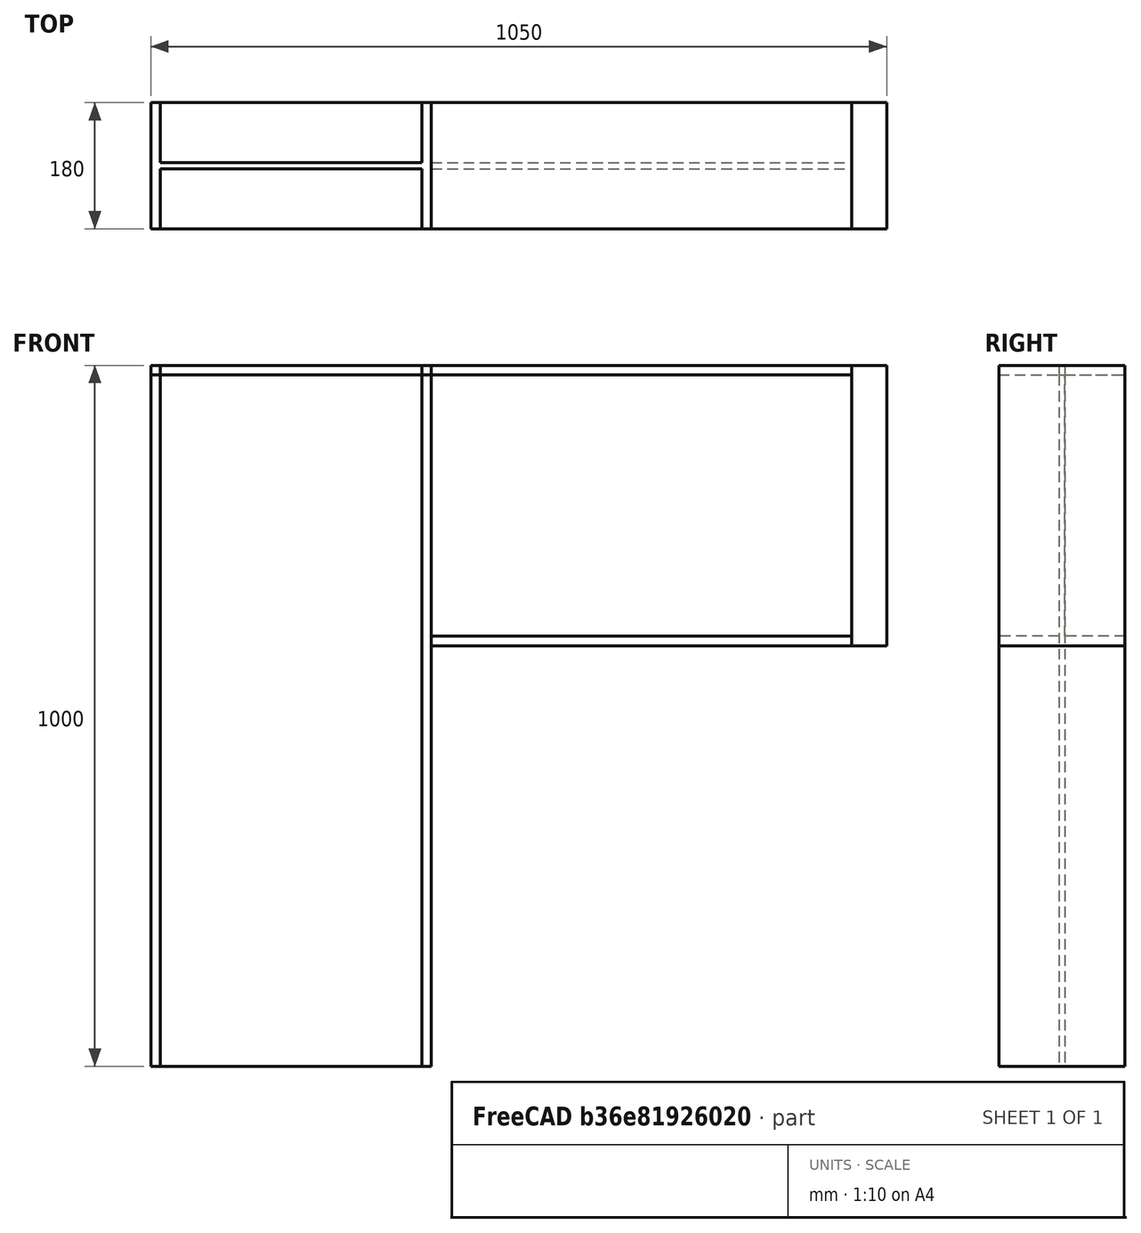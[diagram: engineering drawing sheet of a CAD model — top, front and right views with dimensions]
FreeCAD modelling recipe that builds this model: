
FCSTD DOCUMENT  (FreeCAD 0.21R33771 (Git))
Label: IPE400_3
License: All rights reserved
LicenseURL: http://en.wikipedia.org/wiki/All_rights_reserved
objects: Sketcher::SketchObject×2, Part::Extrusion×2, Part::Box×2, Fem::ConstraintForce×2, Fem::ConstraintFixed×1, App::MaterialObjectPython×1, Fem::FemSolverObjectPython×1, Fem::ConstraintDisplacement×1, Part::FeaturePython×1, Fem::FemMeshObjectPython×1, Fem::FemAnalysis×1
note: 7 computed .brp shape members not serialized (recipe doc carries the construction recipe); baked Part::Feature solids carry a one-line shape summary decoded from their .brp

FEATURE [Sketcher::SketchObject] Sketch
  FullyConstrained = true
  Placement = pos=(0,0,0) rot=(0.57735,0.57735,0.57735;2.0944rad)
  sketch-geometry (12):
    g0: LineSegment StartX=0 StartY=0 StartZ=0 EndX=180 EndY=0 EndZ=0
    g1: LineSegment StartX=180 StartY=0 StartZ=0 EndX=180 EndY=13.5 EndZ=0
    g2: LineSegment StartX=180 StartY=13.5 StartZ=0 EndX=94.3 EndY=13.5 EndZ=0
    g3: LineSegment StartX=94.3 StartY=13.5 StartZ=0 EndX=94.3 EndY=386.5 EndZ=0
    g4: LineSegment StartX=94.3 StartY=386.5 StartZ=0 EndX=180 EndY=386.5 EndZ=0
    g5: LineSegment StartX=180 StartY=386.5 StartZ=0 EndX=180 EndY=400 EndZ=0
    g6: LineSegment StartX=180 StartY=400 StartZ=0 EndX=0 EndY=400 EndZ=0
    g7: LineSegment StartX=0 StartY=400 StartZ=0 EndX=0 EndY=386.5 EndZ=0
    g8: LineSegment StartX=0 StartY=386.5 StartZ=0 EndX=85.7 EndY=386.5 EndZ=0
    g9: LineSegment StartX=85.7 StartY=386.5 StartZ=0 EndX=85.7 EndY=13.5 EndZ=0
    g10: LineSegment StartX=85.7 StartY=13.5 StartZ=0 EndX=0 EndY=13.5 EndZ=0
    g11: LineSegment StartX=0 StartY=13.5 StartZ=0 EndX=0 EndY=0 EndZ=0
  constraints (35):
    c: Coincident(g-1,g0)
    c: PointOnObject(g0,g-1)
    c: Coincident(g0,g1)
    c: Vertical(g1)
    c: Coincident(g1,g2)
    c: Horizontal(g2)
    c: Coincident(g2,g3)
    c: Vertical(g3)
    c: Coincident(g3,g4)
    c: Horizontal(g4)
    c: Coincident(g4,g5)
    c: Vertical(g5)
    c: Coincident(g5,g6)
    c: Horizontal(g6)
    c: Coincident(g6,g7)
    c: Vertical(g7)
    c: Coincident(g7,g8)
    c: Horizontal(g8)
    c: Coincident(g8,g9)
    c: Vertical(g9)
    c: Coincident(g9,g10)
    c: Horizontal(g10)
    c: Coincident(g10,g11)
    c: Coincident(g11,g0)
    c: DistanceX(g0,g0) = 180
    c: DistanceX(g6,g6) = 180
    c: PointOnObject(g6,g-2)
    c: Vertical(g11)
    c: DistanceX(g2,g2) = 85.7
    c: Equal(g10,g2)
    c: DistanceY(g11,g11) = 13.5
    c: Equal(g11,g1)
    c: Equal(g11,g7)
    c: Equal(g11,g5)
    c: DistanceY(g0,g6) = 400
FEATURE [Part::Extrusion] Extrude
  Base = -> Sketch
  Dir = (1,0,0)
  DirMode = 2
  FaceMakerClass = Part::FaceMakerBullseye
  LengthFwd = 600
  LengthRev = 0
  Solid = true
  Symmetric = false
FEATURE [Sketcher::SketchObject] Sketch001
  FullyConstrained = true
  Placement = pos=(0,0,0) rot=(0.57735,0.57735,0.57735;2.0944rad)
  sketch-geometry (12):
    g0: LineSegment StartX=0 StartY=0 StartZ=0 EndX=180 EndY=0 EndZ=0
    g1: LineSegment StartX=180 StartY=0 StartZ=0 EndX=180 EndY=13.5 EndZ=0
    g2: LineSegment StartX=180 StartY=13.5 StartZ=0 EndX=94.3 EndY=13.5 EndZ=0
    g3: LineSegment StartX=94.3 StartY=13.5 StartZ=0 EndX=94.3 EndY=386.5 EndZ=0
    g4: LineSegment StartX=94.3 StartY=386.5 StartZ=0 EndX=180 EndY=386.5 EndZ=0
    g5: LineSegment StartX=180 StartY=386.5 StartZ=0 EndX=180 EndY=400 EndZ=0
    g6: LineSegment StartX=180 StartY=400 StartZ=0 EndX=0 EndY=400 EndZ=0
    g7: LineSegment StartX=0 StartY=400 StartZ=0 EndX=0 EndY=386.5 EndZ=0
    g8: LineSegment StartX=0 StartY=386.5 StartZ=0 EndX=85.7 EndY=386.5 EndZ=0
    g9: LineSegment StartX=85.7 StartY=386.5 StartZ=0 EndX=85.7 EndY=13.5 EndZ=0
    g10: LineSegment StartX=85.7 StartY=13.5 StartZ=0 EndX=0 EndY=13.5 EndZ=0
    g11: LineSegment StartX=0 StartY=13.5 StartZ=0 EndX=0 EndY=0 EndZ=0
  constraints (35):
    c: Coincident(g-1,g0)
    c: PointOnObject(g0,g-1)
    c: Coincident(g0,g1)
    c: Vertical(g1)
    c: Coincident(g1,g2)
    c: Horizontal(g2)
    c: Coincident(g2,g3)
    c: Vertical(g3)
    c: Coincident(g3,g4)
    c: Horizontal(g4)
    c: Coincident(g4,g5)
    c: Vertical(g5)
    c: Coincident(g5,g6)
    c: Horizontal(g6)
    c: Coincident(g6,g7)
    c: Vertical(g7)
    c: Coincident(g7,g8)
    c: Horizontal(g8)
    c: Coincident(g8,g9)
    c: Vertical(g9)
    c: Coincident(g9,g10)
    c: Horizontal(g10)
    c: Coincident(g10,g11)
    c: Coincident(g11,g0)
    c: DistanceX(g0,g0) = 180
    c: DistanceX(g6,g6) = 180
    c: PointOnObject(g6,g-2)
    c: Vertical(g11)
    c: DistanceX(g2,g2) = 85.7
    c: Equal(g10,g2)
    c: DistanceY(g11,g11) = 13.5
    c: Equal(g11,g1)
    c: Equal(g11,g7)
    c: Equal(g11,g5)
    c: DistanceY(g0,g6) = 400
FEATURE [Part::Extrusion] Extrude001
  Base = -> Sketch001
  Dir = (1,0,0)
  DirMode = 2
  FaceMakerClass = Part::FaceMakerBullseye
  LengthFwd = 1000
  LengthRev = 0
  Placement = pos=(-400,0,400) rot=(0,1,0;1.5708rad)
  Solid = true
  Symmetric = false
FEATURE [Part::Box] Box  label="Cube"
  AttacherType = Attacher::AttachEngine3D
  Height = 400
  Length = 50
  Placement = pos=(600,0,0) rot=(0,0,1;0rad)
  Width = 180
FEATURE [Fem::ConstraintForce] ConstraintForce
  Direction = -> Box [Edge12]
  DirectionVector = (1,0,0)
  Force = 1000000
  NormalDirection = (0,0,1)
  Points = (16) [(600,0,400),(616.667,0,400),(633.333,0,400),(650,0,400),(600,60,400),(616.667,60,400),(633.333,60,400),(650,60,400),(600,120,400),(616.667,120,400),+6 more]
  References = -> [Box]
  Scale = 11
FEATURE [Fem::ConstraintFixed] ConstraintFixed
  NormalDirection = (0,0,-1)
  Normals = (8) [(0,0,-1),(0,0,-1),(0,0,-1),(0,0,-1),(0,0,-1),(0,0,-1),(0,0,-1),(0,0,-1)]
  Points = (8) [(-400,180,-600),(0,180,-600),(-400,120,-600),(0,120,-600),(-400,60,-600),(0,60,-600),(-400,0,-600),(0,0,-600)]
  References = -> [Extrude001]
  Scale = 18
FEATURE [App::MaterialObjectPython] MaterialSolid  # material (typed FeaturePython)
  Category = 0
  Material = AuthorAndLicense=(c) 2014 M. Münch - GNU Lesser General Public License (LGPL),CardName=Steel-15CrNi6,Density=7800 kg/m^3,+16 more (map truncated)
FEATURE [Fem::ConstraintForce] ConstraintForce001
  Direction = -> Box [Edge9]
  DirectionVector = (-1,0,0)
  Force = 1000000
  NormalDirection = (0,0,-1)
  Points = (16) [(600,0,0),(616.667,0,0),(633.333,0,0),(650,0,0),(600,60,0),(616.667,60,0),(633.333,60,0),(650,60,0),(600,120,0),(616.667,120,0),(633.333,120,0),+5 more]
  References = -> [Box]
  Reversed = true
  Scale = 11
FEATURE [Fem::FemSolverObjectPython] SolverCcxTools  # FEM object (typed FeaturePython)
  AnalysisType = 0
  BeamShellResultOutput3D = false
  BucklingFactors = 1
  EigenmodeHighLimit = 1000000
  EigenmodeLowLimit = 0
  EigenmodesCount = 10
  GeometricalNonlinearity = 0
  IterationsControlParameterCutb = 0.25,0.5,0.75,0.85,,,1.5,
  IterationsControlParameterIter = 4,8,9,200,10,400,,200,,
  IterationsControlParameterTimeUse = false
  IterationsThermoMechMaximum = 2000
  IterationsUserDefinedIncrementations = false
  IterationsUserDefinedTimeStepLength = false
  MaterialNonlinearity = 0
  MatrixSolverType = 0
  SplitInputWriter = false
  ThermoMechSteadyState = true
  TimeEnd = 1
  TimeInitialStep = 0.01
FEATURE [Fem::ConstraintDisplacement] ConstraintDisplacement
  NormalDirection = (0,1,0)
  Normals = (16) [(0,1,0),(0,1,0),(0,1,0),(0,1,0),(0,1,0),(0,1,0),(0,1,0),(0,1,0),(0,1,0),(0,1,0),(0,1,0),(0,1,0),(0,1,0),(0,1,0),(0,1,0),(0,1,0)]
  Points = (16) [(600,180,0),(600,180,133.333),(600,180,266.667),(600,180,400),(616.667,180,0),(616.667,180,133.333),(616.667,180,266.667),(616.667,180,400),+8 more]
  References = -> [Box]
  Scale = 16
  hasXFormula = false
  hasYFormula = false
  hasZFormula = false
  rotxFix = false
  rotxFree = true
  rotyFix = false
  rotyFree = true
  rotzFix = false
  rotzFree = true
  useFlowSurfaceForce = false
  xDisplacement = 0
  xFix = false
  xFree = true
  xRotation = 0
  yDisplacement = 0
  yFix = false
  yFree = false
  yRotation = 0
  zDisplacement = 0
  zFix = false
  zFree = true
  zRotation = 0
FEATURE [Part::Box] Box002  label="Cube002"
  AttacherType = Attacher::AttachEngine3D
  Height = 13.5
  Length = 400
  Placement = pos=(-400,0,386.5) rot=(0,0,1;0rad)
  Width = 180
FEATURE [Part::FeaturePython] BooleanFragments  # WARN: FeaturePython — macro-defined, semantics opaque (R4)
  Mode = 2
  Objects = -> [Extrude,Extrude001,Box,Box002]
  Tolerance = 0
FEATURE [Fem::FemMeshObjectPython] FEMMeshGmsh  # FEM object (typed FeaturePython)
  Algorithm2D = 0
  Algorithm3D = 0
  CharacteristicLengthMax = 25
  CharacteristicLengthMin = 0
  CoherenceMesh = true
  ElementDimension = 0
  ElementOrder = 1
  GeometryTolerance = 1e-06
  GroupsOfNodes = false
  HighOrderOptimize = 0
  MeshSizeFromCurvature = 12
  OptimizeNetgen = false
  OptimizeStd = true
  Part = -> BooleanFragments
  RecombinationAlgorithm = 0
  Recombine3DAll = false
  RecombineAll = false
  SecondOrderLinear = false
FEATURE [Fem::FemAnalysis] Analysis
  Group = -> [ConstraintForce,ConstraintFixed,MaterialSolid,ConstraintForce001,SolverCcxTools,ConstraintDisplacement,FEMMeshGmsh]
